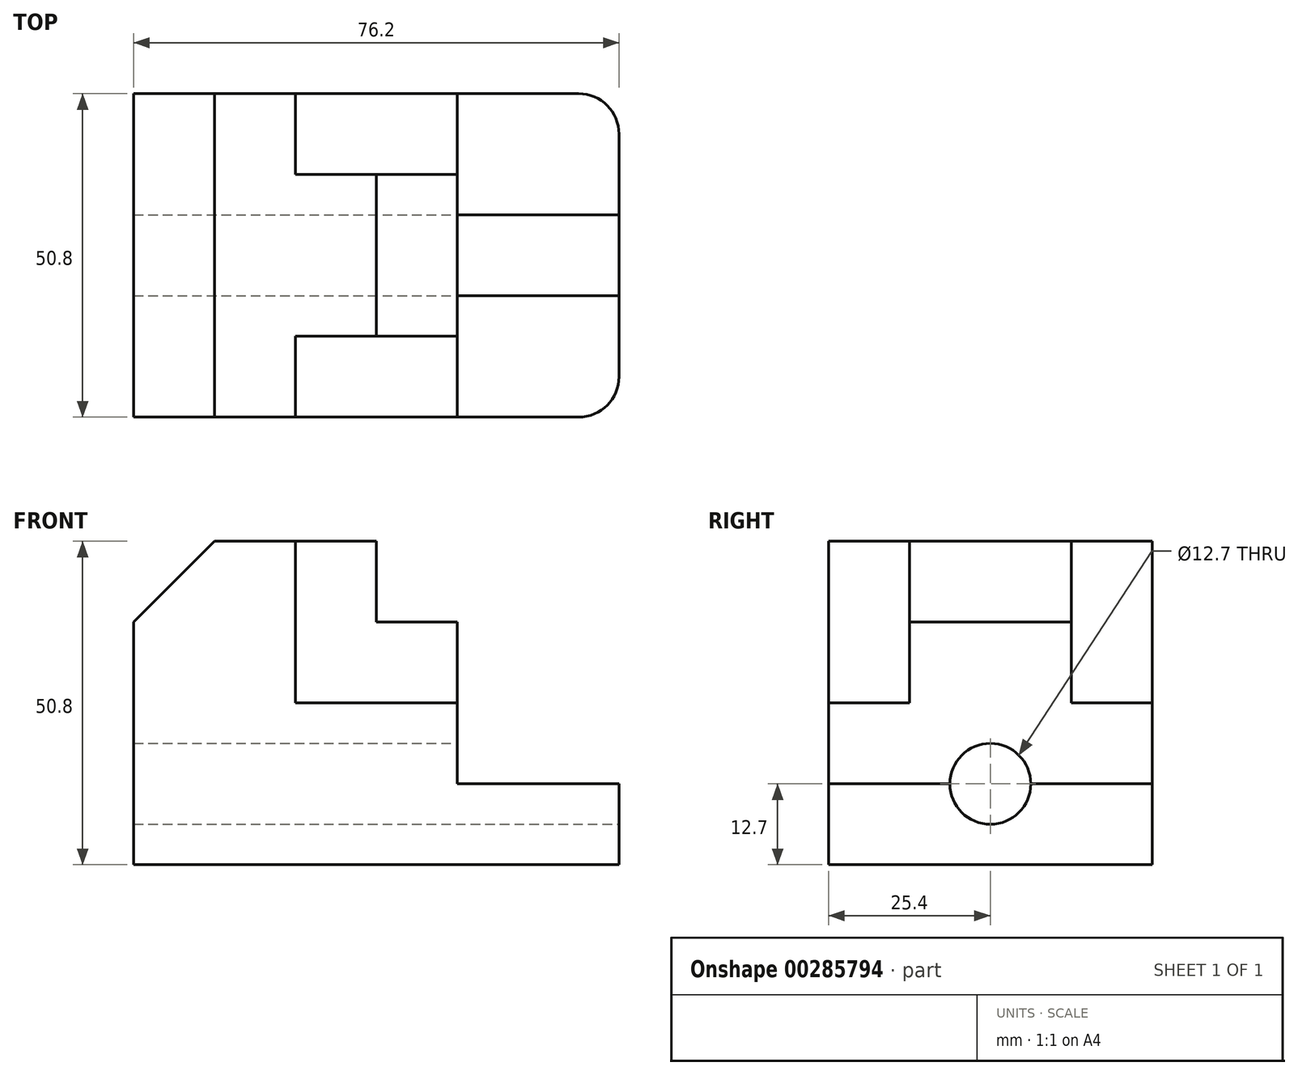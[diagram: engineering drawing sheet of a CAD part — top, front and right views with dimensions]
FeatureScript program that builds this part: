
annotation { "Feature Type Name" : "Feature", "Feature Type Description" : "" }
export const myFeature = defineFeature(function(context is Context, id is Id, definition is map)
    precondition{}
    {
        {
            var Q0;
            Q0=qCreatedBy(makeId("Top.planeOp"),FACE);
            var sketch = newSketch(context, id + "F0", { "sketchPlane" : qUnion([Q0])});
            skLineSegment(sketch, "E0.bottom", {"start": v(0, 0) * mm, "end": v(69.85, 0) * mm});
            skLineSegment(sketch, "E0.top", {"start": v(0, 50.8) * mm, "end": v(69.85, 50.8) * mm});
            skLineSegment(sketch, "E0.left", {"start": v(0, 0) * mm, "end": v(0, 50.8) * mm});
            skLineSegment(sketch, "E0.right", {"start": v(76.2, 6.35) * mm, "end": v(76.2, 44.45) * mm});
            skLineSegment(sketch, "E1", {"start": v(12.7, 50.8) * mm, "end": v(12.7, 0) * mm});
            skLineSegment(sketch, "E2", {"start": v(50.8, 50.8) * mm, "end": v(50.8, 0) * mm});
            skLineSegment(sketch, "E3", {"start": v(25.4, 50.8) * mm, "end": v(25.4, 38.1) * mm});
            skLineSegment(sketch, "E4", {"start": v(25.4, 38.1) * mm, "end": v(50.8, 38.1) * mm});
            skLineSegment(sketch, "E5", {"start": v(50.8, 12.7) * mm, "end": v(25.4, 12.7) * mm});
            skLineSegment(sketch, "E6", {"start": v(25.4, 12.7) * mm, "end": v(25.4, 0) * mm});
            skLineSegment(sketch, "E7", {"start": v(38.1, 38.1) * mm, "end": v(38.1, 12.7) * mm});
            skLineSegment(sketch, "E8", {"start": v(50.8, 31.75) * mm, "end": v(76.2, 31.75) * mm});
            skLineSegment(sketch, "E9", {"start": v(50.8, 19.05) * mm, "end": v(76.2, 19.05) * mm});
            skPoint(sketch, "E10.visualSharp", {"position": v(76.2, 50.8) * mm});
            skArc(sketch, "E10.filletArc", {"start": v(76.2, 44.45) * mm, "mid": v(74.34, 48.94) * mm, "end": v(69.85, 50.8) * mm});
            skPoint(sketch, "E11.visualSharp", {"position": v(76.2, 0) * mm});
            skArc(sketch, "E11.filletArc", {"start": v(69.85, 0) * mm, "mid": v(74.34, 1.86) * mm, "end": v(76.2, 6.35) * mm});
            skSolve(sketch);
        }
        {
            var Q0;
            {var subQ4=sQuery(id+"F0.wireOp",EDGE,"E6");Q0=makeQuery(id+"F0.imprint","IMPRINT",FACE,{"disambiguationData":[TD([[makeQuery(id+"F0.imprint","IMPRINT",EDGE,{"derivedFrom":subQ4}),1.0]])]});}
            extrude(context, id + "F1", {"entities" : qUnion([Q0]), "depth" : 25.4 * mm});
        }
        {
            var Q0;
            {var subQ1=sQuery(id+"F0.wireOp",EDGE,"E1");Q0=makeQuery(id+"F0.imprint","IMPRINT",FACE,{"disambiguationData":[TD([[makeQuery(id+"F0.imprint","IMPRINT",EDGE,{"derivedFrom":subQ1}),1.0]])]});}
            extrude(context, id + "F2", {"entities" : qUnion([Q0]), "operationType" : NewBodyOperationType.ADD, "depth" : 50.8 * mm});
        }
        {
            var Q0;
            {var subQ0=sQuery(id+"F0.wireOp",EDGE,"E0.left");Q0=makeQuery(id+"F0.imprint","IMPRINT",FACE,{"disambiguationData":[TD([[makeQuery(id+"F0.imprint","IMPRINT",EDGE,{"derivedFrom":subQ0}),-1.0]])]});}
            extrude(context, id + "F3", {"entities" : qUnion([Q0]), "operationType" : NewBodyOperationType.ADD, "depth" : 50.8 * mm});
        }
        {
            var Q0;
            {var subQ1=sQuery(id+"F0.wireOp",EDGE,"E3");Q0=makeQuery(id+"F0.imprint","IMPRINT",FACE,{"disambiguationData":[TD([[makeQuery(id+"F0.imprint","IMPRINT",EDGE,{"derivedFrom":subQ1}),1.0]])]});}
            extrude(context, id + "F4", {"entities" : qUnion([Q0]), "operationType" : NewBodyOperationType.ADD, "depth" : 25.4 * mm});
        }
        {
            var Q0;
            {var subQ5=sQuery(id+"F0.wireOp",EDGE,"E9");Q0=makeQuery(id+"F0.imprint","IMPRINT",FACE,{"disambiguationData":[TD([[makeQuery(id+"F0.imprint","IMPRINT",EDGE,{"derivedFrom":subQ5}),-1.0]])]});}
            var Q1;
            {var subQ2=sQuery(id+"F0.wireOp",EDGE,"E8");Q1=makeQuery(id+"F0.imprint","IMPRINT",FACE,{"disambiguationData":[TD([[makeQuery(id+"F0.imprint","IMPRINT",EDGE,{"derivedFrom":subQ2}),1.0]])]});}
            extrude(context, id + "F5", {"entities" : qUnion([Q0, Q1]), "operationType" : NewBodyOperationType.ADD, "depth" : 12.7 * mm});
        }
        {
            var Q0;
            {var subQ0=sQuery(id+"F0.wireOp",EDGE,"E0.bottom");Q0=makeQuery(id+"F5.boolean.opBoolean","MERGE",FACE,{"derivedFrom":[makeQuery(id+"F3.boolean.opBoolean","MERGE",FACE,{"derivedFrom":[makeQuery(id+"F2.boolean.opBoolean","MERGE",FACE,{"derivedFrom":[makeQuery(id+"F1.opExtrude","SWEPT_FACE",FACE,{"disambiguationData":[OSD([subQ0])]}),makeQuery(id+"F2.opExtrude","SWEPT_FACE",FACE,{"disambiguationData":[OSD([subQ0])]})]}),makeQuery(id+"F3.opExtrude","SWEPT_FACE",FACE,{"disambiguationData":[OSD([subQ0])]})]}),makeQuery(id+"F5.opExtrude","SWEPT_FACE",FACE,{"disambiguationData":[OSD([subQ0])]})]});}
            var sketch = newSketch(context, id + "F6", { "sketchPlane" : qUnion([Q0])});
            skLineSegment(sketch, "E12", {"start": v(0, 50.8) * mm, "end": v(0, 38.1) * mm});
            skLineSegment(sketch, "E13", {"start": v(0, 38.1) * mm, "end": v(12.7, 50.8) * mm});
            skLineSegment(sketch, "E14", {"start": v(12.7, 50.8) * mm, "end": v(0, 50.8) * mm});
            skSolve(sketch);
        }
        {
            var Q0;
            Q0 = qSketchRegion(id + "F6", true);
            extrude(context, id + "F7", {"entities" : qUnion([Q0]), "operationType" : NewBodyOperationType.REMOVE, "endBound" : BoundingType.THROUGH_ALL, "oppositeDirection" : true, "depth" : 25.4 * mm});
        }
        {
            var Q0;
            {var subQ6=sQuery(id+"F0.wireOp",EDGE,"E7");Q0=makeQuery(id+"F0.imprint","IMPRINT",FACE,{"disambiguationData":[TD([[makeQuery(id+"F0.imprint","IMPRINT",EDGE,{"derivedFrom":subQ6}),1.0]])]});}
            extrude(context, id + "F8", {"entities" : qUnion([Q0]), "operationType" : NewBodyOperationType.ADD, "depth" : 38.1 * mm});
        }
        {
            var Q0;
            {var subQ0=sQuery(id+"F0.wireOp",EDGE,"E8");Q0=makeQuery(id+"F0.imprint","IMPRINT",FACE,{"disambiguationData":[TD([[makeQuery(id+"F0.imprint","IMPRINT",EDGE,{"derivedFrom":subQ0}),-1.0]])]});}
            extrude(context, id + "F9", {"entities" : qUnion([Q0]), "operationType" : NewBodyOperationType.ADD, "depth" : 12.7 * mm});
        }
        {
            var Q0;
            {var subQ0=sQuery(id+"F0.wireOp",EDGE,"E8");Q0=makeQuery(id+"F0.imprint","IMPRINT",FACE,{"disambiguationData":[TD([[makeQuery(id+"F0.imprint","IMPRINT",EDGE,{"derivedFrom":subQ0}),-1.0]])]});}
            extrude(context, id + "F10", {"entities" : qUnion([Q0]), "operationType" : NewBodyOperationType.REMOVE, "endBound" : BoundingType.THROUGH_ALL, "oppositeDirection" : true, "depth" : 25.4 * mm});
        }
        {
            var Q0;
            {var subQ0=sQuery(id+"F0.wireOp",EDGE,"E8");Q0=makeQuery(id+"F0.imprint","IMPRINT",FACE,{"disambiguationData":[TD([[makeQuery(id+"F0.imprint","IMPRINT",EDGE,{"derivedFrom":subQ0}),-1.0]])]});}
            extrude(context, id + "F11", {"entities" : qUnion([Q0]), "operationType" : NewBodyOperationType.REMOVE, "endBound" : BoundingType.THROUGH_ALL, "depth" : 25.4 * mm});
        }
        {
            var Q0;
            {var subQ0=sQuery(id+"F0.wireOp",EDGE,"E8");Q0=makeQuery(id+"F0.imprint","IMPRINT",FACE,{"disambiguationData":[TD([[makeQuery(id+"F0.imprint","IMPRINT",EDGE,{"derivedFrom":subQ0}),-1.0]])]});}
            extrude(context, id + "F12", {"entities" : qUnion([Q0]), "operationType" : NewBodyOperationType.ADD, "depth" : 12.7 * mm});
        }
        {
            var Q0;
            {var subQ0=sQuery(id+"F0.wireOp",EDGE,"E0.right");var subQ6=sQuery(id+"F0.wireOp",EDGE,"E10.filletArc");var subQ12=sQuery(id+"F0.wireOp",EDGE,"E11.filletArc");var subQ25=makeQuery(id+"F9.boolean.opBoolean","MERGE",FACE,{"derivedFrom":[makeQuery(id+"F5.opExtrude","SWEPT_FACE",FACE,{"disambiguationData":[OSD([subQ0]),TDD([makeQuery(id+"F0.imprint","IMPRINT",EDGE,{"disambiguationData":[TD([[makeQuery(id+"F0.imprint","INTERSECT",VERTEX,{"derivedFrom":[subQ0,subQ12]}),-1.0]])],"derivedFrom":subQ0})])]}),makeQuery(id+"F5.opExtrude","SWEPT_FACE",FACE,{"disambiguationData":[OSD([subQ0]),TDD([makeQuery(id+"F0.imprint","IMPRINT",EDGE,{"disambiguationData":[TD([[makeQuery(id+"F0.imprint","INTERSECT",VERTEX,{"derivedFrom":[subQ0,subQ6]}),1.0]])],"derivedFrom":subQ0})])]}),makeQuery(id+"F9.opExtrude","SWEPT_FACE",FACE,{"disambiguationData":[OSD([subQ0])]})]});Q0=makeQuery(id+"F12.boolean.opBoolean","MERGE",FACE,{"derivedFrom":[makeQuery(id+"F11.boolean.opBoolean","SPLIT",FACE,{"disambiguationData":[TD([makeQuery(id+"F5.opExtrude","SWEPT_FACE",FACE,{"disambiguationData":[OSD([subQ12])]})])],"derivedFrom":subQ25}),makeQuery(id+"F11.boolean.opBoolean","SPLIT",FACE,{"disambiguationData":[TD([makeQuery(id+"F5.opExtrude","SWEPT_FACE",FACE,{"disambiguationData":[OSD([subQ6])]})])],"derivedFrom":subQ25}),makeQuery(id+"F12.opExtrude","SWEPT_FACE",FACE,{"disambiguationData":[OSD([subQ0])]})]});}
            var sketch = newSketch(context, id + "F13", { "sketchPlane" : qUnion([Q0])});
            skCircle(sketch, "E15", {"center": v(25.4, 12.7) * mm, "radius": 6.35 * mm});
            skSolve(sketch);
        }
        {
            var Q0;
            Q0 = qSketchRegion(id + "F13", true);
            var Q1;
            {var subQ0=sQuery(id+"F0.wireOp",EDGE,"E2");Q1=makeQuery(id+"F11.boolean.opBoolean","MERGE",FACE,{"derivedFrom":[makeQuery(id+"F8.boolean.opBoolean","MERGE",FACE,{"derivedFrom":[makeQuery(id+"F1.opExtrude","SWEPT_FACE",FACE,{"disambiguationData":[OSD([subQ0])]}),makeQuery(id+"F4.opExtrude","SWEPT_FACE",FACE,{"disambiguationData":[OSD([subQ0])]}),makeQuery(id+"F8.opExtrude","SWEPT_FACE",FACE,{"disambiguationData":[OSD([subQ0])]})]}),makeQuery(id+"F11.opExtrude","SWEPT_FACE",FACE,{"disambiguationData":[OSD([subQ0])]})]});}
            extrude(context, id + "F14", {"entities" : qUnion([Q0]), "operationType" : NewBodyOperationType.REMOVE, "endBound" : BoundingType.THROUGH_ALL, "oppositeDirection" : true, "endBoundEntityFace" : qUnion([Q1]), "depth" : 25.4 * mm});
        }
    });
